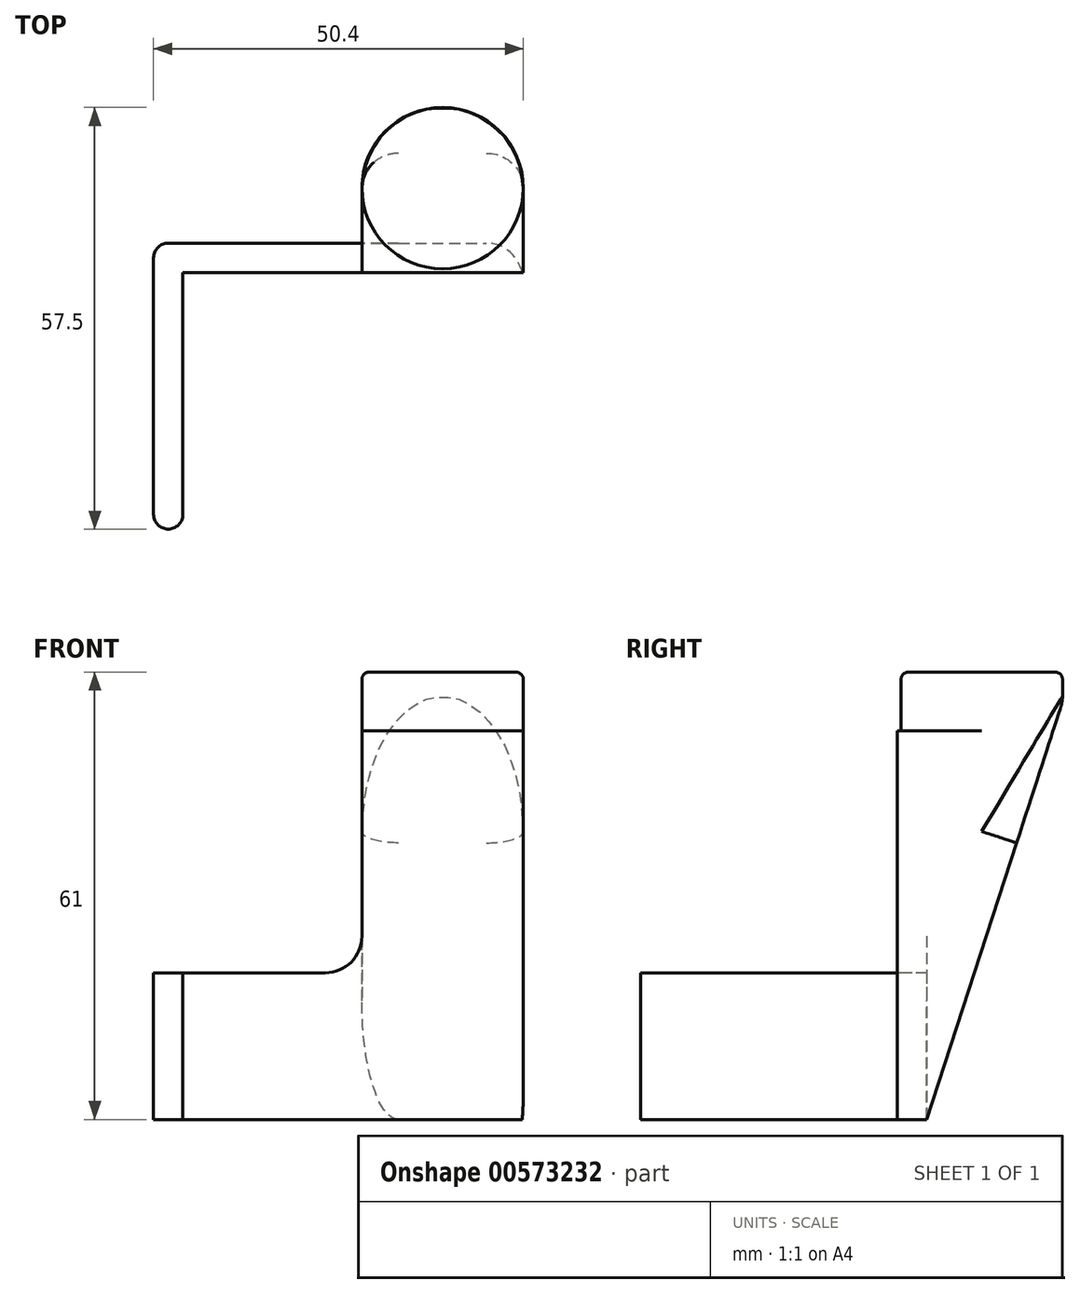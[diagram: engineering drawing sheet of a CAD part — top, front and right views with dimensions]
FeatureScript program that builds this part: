
annotation { "Feature Type Name" : "Feature", "Feature Type Description" : "" }
export const myFeature = defineFeature(function(context is Context, id is Id, definition is map)
    precondition{}
    {
        {
            var Q0;
            Q0=qCreatedBy(makeId("Top.planeOp"),FACE);
            var sketch = newSketch(context, id + "F0", { "sketchPlane" : qUnion([Q0])});
            skCircle(sketch, "E0", {"center": v(-2.72, 25.03) * mm, "radius": 11 * mm});
            skLineSegment(sketch, "E1.bottom", {"start": v(8.28, 13.53) * mm, "end": v(-13.72, 13.53) * mm});
            skLineSegment(sketch, "E1.left", {"start": v(8.28, 13.53) * mm, "end": v(8.28, 25.03) * mm});
            skLineSegment(sketch, "E1.right", {"start": v(-13.72, 13.53) * mm, "end": v(-13.72, 25.03) * mm});
            skLineSegment(sketch, "E2.top", {"start": v(-13.72, 13.53) * mm, "end": v(-42.12, 13.53) * mm});
            skLineSegment(sketch, "E2.left", {"start": v(-13.72, 25.03) * mm, "end": v(-13.72, 19.53) * mm});
            skLineSegment(sketch, "E3.bottom", {"start": v(-42.12, 13.53) * mm, "end": v(-38.12, 13.53) * mm});
            skLineSegment(sketch, "E3.top", {"start": v(-40.12, -21.47) * mm, "end": v(-40.12, -21.47) * mm});
            skLineSegment(sketch, "E3.left", {"start": v(-42.12, 13.53) * mm, "end": v(-42.12, -19.47) * mm});
            skLineSegment(sketch, "E3.right", {"start": v(-38.12, 13.53) * mm, "end": v(-38.12, -19.47) * mm});
            skLineSegment(sketch, "E4.bottom", {"start": v(8.28, 13.53) * mm, "end": v(4.28, 13.53) * mm});
            skLineSegment(sketch, "E4.top", {"start": v(6.28, -21.47) * mm, "end": v(6.28, -21.47) * mm});
            skLineSegment(sketch, "E4.left", {"start": v(8.28, 13.53) * mm, "end": v(8.28, -19.47) * mm});
            skLineSegment(sketch, "E4.right", {"start": v(4.28, 13.53) * mm, "end": v(4.28, -19.47) * mm});
            skLineSegment(sketch, "E5.top", {"start": v(-15.72, 17.53) * mm, "end": v(-40.12, 17.53) * mm});
            skLineSegment(sketch, "E5.left", {"start": v(-13.72, 13.53) * mm, "end": v(-13.72, 17.53) * mm});
            skLineSegment(sketch, "E5.right", {"start": v(-42.12, 13.53) * mm, "end": v(-42.12, 15.53) * mm});
            skPoint(sketch, "E6.visualSharp", {"position": v(-42.12, -21.47) * mm});
            skArc(sketch, "E6.filletArc", {"start": v(-42.12, -19.47) * mm, "mid": v(-41.53, -20.88) * mm, "end": v(-40.12, -21.47) * mm});
            skPoint(sketch, "E7.visualSharp", {"position": v(-38.12, -21.47) * mm});
            skArc(sketch, "E7.filletArc", {"start": v(-40.12, -21.47) * mm, "mid": v(-38.7, -20.88) * mm, "end": v(-38.12, -19.47) * mm});
            skPoint(sketch, "E8.visualSharp", {"position": v(-42.12, 17.53) * mm});
            skArc(sketch, "E8.filletArc", {"start": v(-40.12, 17.53) * mm, "mid": v(-41.53, 16.94) * mm, "end": v(-42.12, 15.53) * mm});
            skPoint(sketch, "E9.visualSharp", {"position": v(8.28, -21.47) * mm});
            skArc(sketch, "E9.filletArc", {"start": v(6.28, -21.47) * mm, "mid": v(7.7, -20.88) * mm, "end": v(8.28, -19.47) * mm});
            skPoint(sketch, "E10.visualSharp", {"position": v(4.28, -21.47) * mm});
            skArc(sketch, "E10.filletArc", {"start": v(4.28, -19.47) * mm, "mid": v(4.87, -20.88) * mm, "end": v(6.28, -21.47) * mm});
            skLineSegment(sketch, "E11", {"start": v(-15.72, 17.53) * mm, "end": v(-13.72, 17.53) * mm});
            skSolve(sketch);
        }
        {
            var Q0;
            {var subQ1=sQuery(id+"F0.wireOp",EDGE,"E3.left");Q0=makeQuery(id+"F0.imprint","IMPRINT",FACE,{"disambiguationData":[TD([[makeQuery(id+"F0.imprint","IMPRINT",EDGE,{"derivedFrom":subQ1}),1.0]])]});}
            var Q1;
            Q1=makeQuery(id+"F0.imprint","IMPRINT",FACE,{"disambiguationData":[TD([[makeQuery(id+"F0.imprint","IMPRINT",EDGE,{"derivedFrom":sQuery(id+"F0.wireOp",EDGE,"E4.bottom")}),1.0]])]});
            var Q2;
            Q2=makeQuery(id+"F0.imprint","IMPRINT",FACE,{"disambiguationData":[TD([[makeQuery(id+"F0.imprint","IMPRINT",EDGE,{"derivedFrom":sQuery(id+"F0.wireOp",EDGE,"E1.right")}),1.0]])]});
            var Q3;
            Q3=makeQuery(id+"F0.imprint","IMPRINT",FACE,{"disambiguationData":[TD([[makeQuery(id+"F0.imprint","IMPRINT",EDGE,{"derivedFrom":sQuery(id+"F0.wireOp",EDGE,"E1.bottom")}),-1.0]])]});
            var Q4;
            {var subQ0=sQuery(id+"F0.wireOp",EDGE,"E0");var subQ1=makeQuery(id+"F0.imprint","INTERSECT",VERTEX,{"derivedFrom":[subQ0,sQuery(id+"F0.wireOp",EDGE,"E1.left")]});Q4=makeQuery(id+"F0.imprint","IMPRINT",FACE,{"disambiguationData":[TD([[makeQuery(id+"F0.imprint","IMPRINT",EDGE,{"disambiguationData":[TD([[subQ1,-1.0]])],"derivedFrom":subQ0}),1.0]])]});}
            var Q5;
            Q5=makeQuery(id+"F0.imprint","IMPRINT",FACE,{"disambiguationData":[TD([[makeQuery(id+"F0.imprint","IMPRINT",EDGE,{"derivedFrom":sQuery(id+"F0.wireOp",EDGE,"E5.top")}),1.0]])]});
            extrude(context, id + "F1", {"entities" : qUnion([Q0, Q1, Q2, Q3, Q4, Q5]), "depth" : 20 * mm, "offsetDistance" : 25 * mm});
        }
        {
            var Q0;
            Q0=makeQuery(id+"F0.imprint","IMPRINT",FACE,{"disambiguationData":[TD([[makeQuery(id+"F0.imprint","IMPRINT",EDGE,{"derivedFrom":sQuery(id+"F0.wireOp",EDGE,"E1.bottom")}),-1.0]])]});
            var Q1;
            {var subQ0=sQuery(id+"F0.wireOp",EDGE,"E0");var subQ1=makeQuery(id+"F0.imprint","INTERSECT",VERTEX,{"derivedFrom":[subQ0,sQuery(id+"F0.wireOp",EDGE,"E1.left")]});Q1=makeQuery(id+"F0.imprint","IMPRINT",FACE,{"disambiguationData":[TD([[makeQuery(id+"F0.imprint","IMPRINT",EDGE,{"disambiguationData":[TD([[subQ1,-1.0]])],"derivedFrom":subQ0}),1.0]])]});}
            extrude(context, id + "F2", {"entities" : qUnion([Q0, Q1]), "operationType" : NewBodyOperationType.ADD, "depth" : (20 + 33) * mm, "offsetDistance" : 25 * mm});
        }
        {
            var Q0;
            {var subQ0=sQuery(id+"F0.wireOp",EDGE,"E0");var subQ1=makeQuery(id+"F0.imprint","INTERSECT",VERTEX,{"derivedFrom":[subQ0,sQuery(id+"F0.wireOp",EDGE,"E1.left")]});Q0=makeQuery(id+"F0.imprint","IMPRINT",FACE,{"disambiguationData":[TD([[makeQuery(id+"F0.imprint","IMPRINT",EDGE,{"disambiguationData":[TD([[subQ1,-1.0]])],"derivedFrom":subQ0}),1.0]])]});}
            extrude(context, id + "F3", {"entities" : qUnion([Q0]), "operationType" : NewBodyOperationType.ADD, "depth" : (20 + 33 + 8) * mm, "offsetDistance" : 25 * mm});
        }
        {
            var Q0;
            {var subQ0=sQuery(id+"F0.wireOp",EDGE,"E2.left");Q0=makeQuery(id+"F2.boolean.opBoolean","INTERSECT",EDGE,{"derivedFrom":[makeQuery(id+"F1.opExtrude","CAP_FACE",FACE,{"disambiguationData":[OSD([sQuery(id+"F0.wireOp",EDGE,"E0"),sQuery(id+"F0.wireOp",EDGE,"E1.bottom"),sQuery(id+"F0.wireOp",EDGE,"E1.left"),subQ0,sQuery(id+"F0.wireOp",EDGE,"E3.left"),sQuery(id+"F0.wireOp",EDGE,"E3.right"),sQuery(id+"F0.wireOp",EDGE,"E4.left"),sQuery(id+"F0.wireOp",EDGE,"E4.right"),sQuery(id+"F0.wireOp",EDGE,"E2.top"),sQuery(id+"F0.wireOp",EDGE,"E5.top"),sQuery(id+"F0.wireOp",EDGE,"E5.right"),sQuery(id+"F0.wireOp",EDGE,"E6.filletArc"),sQuery(id+"F0.wireOp",EDGE,"E7.filletArc"),sQuery(id+"F0.wireOp",EDGE,"E8.filletArc"),sQuery(id+"F0.wireOp",EDGE,"E9.filletArc"),sQuery(id+"F0.wireOp",EDGE,"E10.filletArc"),sQuery(id+"F0.wireOp",EDGE,"fd9f3246-6cb5-476c-9d88-f0f1528356f3.filletArc")])],"isStart":false}),makeQuery(id+"F2.opExtrude","SWEPT_FACE",FACE,{"disambiguationData":[OSD([sQuery(id+"F0.wireOp",EDGE,"E1.right"),subQ0,sQuery(id+"F0.wireOp",EDGE,"E5.left")])]})]});}
            var Q1;
            {var subQ0=sQuery(id+"F0.wireOp",EDGE,"E1.bottom");Q1=makeQuery(id+"F2.boolean.opBoolean","INTERSECT",EDGE,{"derivedFrom":[makeQuery(id+"F1.opExtrude","CAP_FACE",FACE,{"disambiguationData":[OSD([sQuery(id+"F0.wireOp",EDGE,"E0"),subQ0,sQuery(id+"F0.wireOp",EDGE,"E1.left"),sQuery(id+"F0.wireOp",EDGE,"E2.left"),sQuery(id+"F0.wireOp",EDGE,"E3.left"),sQuery(id+"F0.wireOp",EDGE,"E3.right"),sQuery(id+"F0.wireOp",EDGE,"E4.left"),sQuery(id+"F0.wireOp",EDGE,"E4.right"),sQuery(id+"F0.wireOp",EDGE,"E2.top"),sQuery(id+"F0.wireOp",EDGE,"E5.top"),sQuery(id+"F0.wireOp",EDGE,"E5.right"),sQuery(id+"F0.wireOp",EDGE,"E6.filletArc"),sQuery(id+"F0.wireOp",EDGE,"E7.filletArc"),sQuery(id+"F0.wireOp",EDGE,"E8.filletArc"),sQuery(id+"F0.wireOp",EDGE,"E9.filletArc"),sQuery(id+"F0.wireOp",EDGE,"E10.filletArc"),sQuery(id+"F0.wireOp",EDGE,"fd9f3246-6cb5-476c-9d88-f0f1528356f3.filletArc")])],"isStart":false}),makeQuery(id+"F2.opExtrude","SWEPT_FACE",FACE,{"disambiguationData":[OSD([subQ0,sQuery(id+"F0.wireOp",EDGE,"E4.bottom")])]})]});}
            fillet(context, id + "F4", {"entities" : qUnion([Q0, Q1]), "radius" : 5 * mm, "tangentPropagation" : true, "allowEdgeOverflow" : false});
        }
        {
            var Q0;
            Q0=makeQuery(id+"F3.opExtrude","CAP_EDGE",EDGE,{"disambiguationData":[OSD([sQuery(id+"F0.wireOp",EDGE,"E0")])],"isStart":false});
            fillet(context, id + "F5", {"entities" : qUnion([Q0]), "radius" : 1 * mm, "tangentPropagation" : true, "allowEdgeOverflow" : false});
        }
        {
            var Q0;
            Q0=sQuery(id+"F0.wireOp",EDGE,"E5.top");
            cPlane(context, id + "F6", {"entities" : qUnion([Q0]), "cplaneType" : CPlaneType.LINE_ANGLE, "offset" : 25 * mm, "angle" : 18 * degree, "width" : 150 * mm, "height" : 150 * mm});
        }
        {
            var Q0;
            Q0=qCreatedBy(id+"F6.planeOp",FACE);
            var sketch = newSketch(context, id + "F7", { "sketchPlane" : qUnion([Q0])});
            skLineSegment(sketch, "E12.bottom", {"start": v(-42.21, -1.48) * mm, "end": v(21.35, -1.48) * mm});
            skLineSegment(sketch, "E12.top", {"start": v(-42.21, 74.42) * mm, "end": v(21.35, 74.42) * mm});
            skLineSegment(sketch, "E12.left", {"start": v(-42.21, -1.48) * mm, "end": v(-42.21, 74.42) * mm});
            skLineSegment(sketch, "E12.right", {"start": v(21.35, -1.48) * mm, "end": v(21.35, 74.42) * mm});
            skSolve(sketch);
        }
        {
            var Q0;
            Q0 = qSketchRegion(id + "F7", true);
            extrude(context, id + "F8", {"entities" : qUnion([Q0]), "operationType" : NewBodyOperationType.REMOVE, "oppositeDirection" : true, "depth" : 25 * mm, "offsetDistance" : 25 * mm});
        }
        {
            var Q0;
            {var subQ0=sQuery(id+"F0.wireOp",EDGE,"E0");Q0=makeQuery(id+"F8.boolean.opBoolean","INTERSECT",EDGE,{"derivedFrom":[makeQuery(id+"F3.boolean.opBoolean","MERGE",FACE,{"derivedFrom":[makeQuery(id+"F2.boolean.opBoolean","MERGE",FACE,{"derivedFrom":[makeQuery(id+"F1.opExtrude","SWEPT_FACE",FACE,{"disambiguationData":[OSD([subQ0])]}),makeQuery(id+"F2.opExtrude","SWEPT_FACE",FACE,{"disambiguationData":[OSD([subQ0])]})]}),makeQuery(id+"F3.opExtrude","SWEPT_FACE",FACE,{"disambiguationData":[OSD([subQ0])]})]}),makeQuery(id+"F8.opExtrude","CAP_FACE",FACE,{"disambiguationData":[OSD([sQuery(id+"F7.wireOp",EDGE,"E12.bottom"),sQuery(id+"F7.wireOp",EDGE,"E12.top"),sQuery(id+"F7.wireOp",EDGE,"E12.left"),sQuery(id+"F7.wireOp",EDGE,"E12.right")])],"isStart":true})]});}
            fillet(context, id + "F9", {"entities" : qUnion([Q0]), "radius" : 5 * mm, "tangentPropagation" : true, "allowEdgeOverflow" : false});
        }
    });
